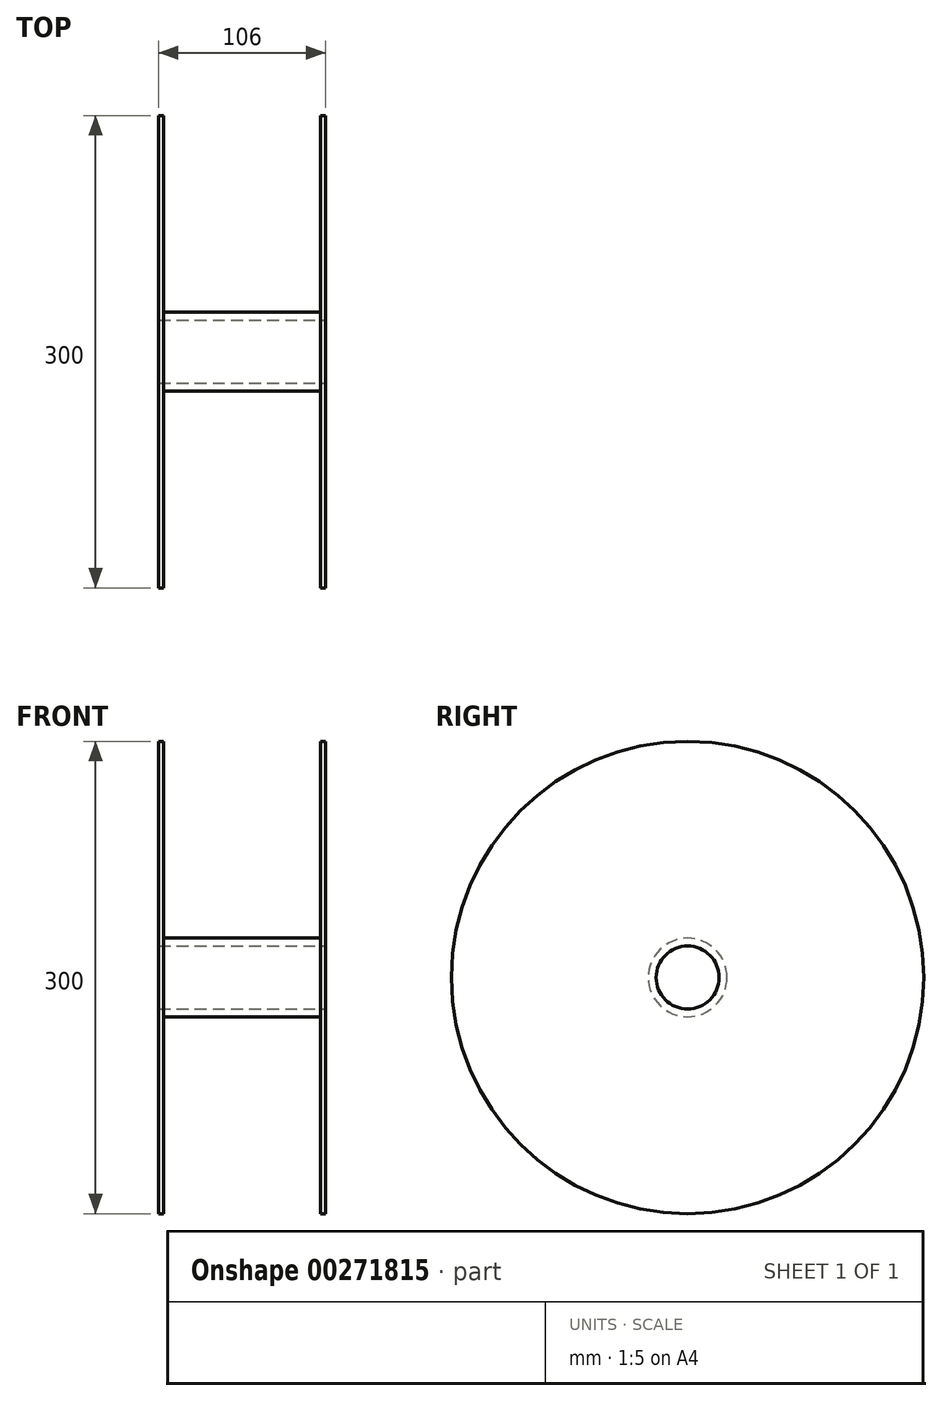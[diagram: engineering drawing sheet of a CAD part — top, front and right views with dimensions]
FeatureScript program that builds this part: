
annotation { "Feature Type Name" : "Feature", "Feature Type Description" : "" }
export const myFeature = defineFeature(function(context is Context, id is Id, definition is map)
    precondition{}
    {
        {
            var Q0;
            Q0=qCreatedBy(makeId("Front.planeOp"),FACE);
            var sketch = newSketch(context, id + "F0", { "sketchPlane" : qUnion([Q0])});
            skLineSegment(sketch, "E0", {"start": v(0, 25) * mm, "end": v(50, 25) * mm});
            skLineSegment(sketch, "E1", {"start": v(50, 25) * mm, "end": v(50, 150) * mm});
            skLineSegment(sketch, "E2", {"start": v(50, 150) * mm, "end": v(53, 150) * mm});
            skLineSegment(sketch, "E3", {"start": v(53, 150) * mm, "end": v(53, 0) * mm});
            skLineSegment(sketch, "E4", {"start": v(0, 0) * mm, "end": v(117.13, 0) * mm, "construction": true});
            skLineSegment(sketch, "E5", {"start": v(53, 0) * mm, "end": v(0, 0) * mm});
            skLineSegment(sketch, "E6", {"start": v(0, 25) * mm, "end": v(0, 87.4) * mm, "construction": true});
            skLineSegment(sketch, "E7.MirrorCS", {"start": v(-50, 150) * mm, "end": v(-53, 150) * mm});
            skLineSegment(sketch, "E8.MirrorCS", {"start": v(-53, 0) * mm, "end": v(0, 0) * mm});
            skLineSegment(sketch, "E9.MirrorCS", {"start": v(-53, 150) * mm, "end": v(-53, 0) * mm});
            skLineSegment(sketch, "E10.MirrorCS", {"start": v(0, 0) * mm, "end": v(-117.13, 0) * mm, "construction": true});
            skLineSegment(sketch, "E11.MirrorCS", {"start": v(-50, 25) * mm, "end": v(-50, 150) * mm});
            skLineSegment(sketch, "E12.MirrorCS", {"start": v(0, 25) * mm, "end": v(-50, 25) * mm});
            skSolve(sketch);
        }
        {
            var Q0;
            Q0=qSketchRegion(id+"F0",true);
            var Q1;
            Q1=sQuery(id+"F0.wireOp",EDGE,"E4");
            revolve(context, id + "F1", {"entities" : qUnion([Q0]), "axis" : qUnion([Q1]), "revolveType" : RevolveType.FULL});
        }
        {
            var Q0;
            Q0=makeQuery(id+"F1.opRevolve","SWEPT_FACE",FACE,{"disambiguationData":[OSD([sQuery(id+"F0.wireOp",EDGE,"E3")])]});
            var sketch = newSketch(context, id + "F2", { "sketchPlane" : qUnion([Q0])});
            skPoint(sketch, "E13", {"position": v(0, 0) * mm});
            skSolve(sketch);
        }
        {
            var Q0;
            Q0=sQuery(id+"F2.wireOp",VERTEX,"E13");
            var Q1;
            Q1=makeQuery(id+"F1.opRevolve","SWEPT_BODY",BODY,{"disambiguationData":[OSD([sQuery(id+"F0.wireOp",EDGE,"E0"),sQuery(id+"F0.wireOp",EDGE,"E1"),sQuery(id+"F0.wireOp",EDGE,"E2"),sQuery(id+"F0.wireOp",EDGE,"E3"),sQuery(id+"F0.wireOp",EDGE,"E5"),sQuery(id+"F0.wireOp",EDGE,"E7.MirrorCS"),sQuery(id+"F0.wireOp",EDGE,"E8.MirrorCS"),sQuery(id+"F0.wireOp",EDGE,"E9.MirrorCS"),sQuery(id+"F0.wireOp",EDGE,"E11.MirrorCS"),sQuery(id+"F0.wireOp",EDGE,"E12.MirrorCS")])]});
            hole(context, id + "F3", {"style" : HoleStyle.SIMPLE, "endStyle" : HoleEndStyle.THROUGH, "holeDiameter" : 40 * mm, "startFromSketch" : true, "locations" : qUnion([Q0]), "scope" : qUnion([Q1]), "isTappedThrough" : true});
        }
    });
